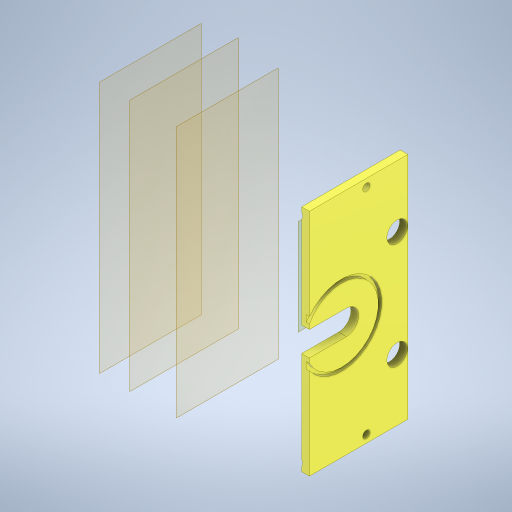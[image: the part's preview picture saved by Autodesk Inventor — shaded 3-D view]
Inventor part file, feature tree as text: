
AUTODESK INVENTOR PART (.ipt)
format: ipt  version: 2023 (Build 270158030, 158C)  size: 688,128 bytes
history: native  units: mm
features: sketch x18, extrude x17, projected_geometry x5, hole x4, plane x3, mirror x2, split x1
ambient origin geometry x8: Origin, YZ Plane, XZ Plane, XY Plane, X Axis, Y Axis, Z Axis, Center Point
bodies: Solid1 (feature_tree)
feature tree (50):
  extrude  "MainInnerBodyExtrusion"  Depth=149.0mm
  extrude  "HoleForCamerabase"  Depth=15.7mm
  extrude  "HoleForFan"  Depth=59.0mm
  extrude  "HoleForPi"  TaperAngle=0.0deg  [1 undecoded]
  extrude  "HoleForPoeAdapter"  Depth=62.0mm
  extrude  "HoleForThermister"  Depth=47.0mm
  extrude  "HoleForSensor"  Depth=32.0mm
  extrude  "SlotsForRearFan"  Depth=47.0mm
  extrude  "VentForCamera"  Depth=16.0mm
  extrude  "HoleForLens"  Depth=118.0mm
  sketch  "Sketch23"  dims[d26=49.0mm d27=118.0mm]
  hole  "Hole for 6-32 Insert"  [1 undecoded]
  hole  "Screw hole for 6-32 screw"  [1 undecoded]
  hole  "Side hole for 1-4 20 insert"  [1 undecoded]
  mirror  "Mirror for side insert"
  extrude  "Extrusion18"  Depth=17.0mm
  extrude  "HoleForPowerWire"  TaperAngle=0.0deg  [1 undecoded]
  extrude  "Extrusion21"  Depth=2.0mm
  extrude  "Extrusion22"  Depth=4.0mm
  extrude  "Extrusion23"  Depth=10.0mm
  extrude  "ExtrusionForBottom"  Depth=10.0mm TaperAngle=0.0deg
  hole  "10-32 holesToBoltFixture"  [1 undecoded]
  plane  "Work Plane1"
  plane  "Work Plane2"
  mirror  "Mirror4"
  extrude  "CutOutForFilter"  Depth=10.0mm
  plane  "Work Plane3"
  split  "Split2"
  sketch  "Sketch1"  dims[d0=222.7mm d1=149.0mm]
  sketch  "Sketch3"  dims[d2=50.0mm d3=0.0mm d5=15.7mm]
  sketch  "Sketch4"  dims[d6=54.0mm d7=59.0mm]
  sketch  "Sketch6"  dims[d8=47.0mm d9=0.0mm]
  sketch  "Sketch7"  dims[d13=16.0mm d14=62.0mm]
  sketch  "Sketch11"  dims[d15=3.0mm d16=47.0mm]
  sketch  "Sketch15"  dims[d17=0.0mm d20=32.0mm]
  sketch  "Sketch16"  dims[d21=129.0mm d22=47.0mm]
  sketch  "Sketch18"  dims[d23=0.0mm d25=16.0mm]
  sketch  "Sketch24"  dims[d28=47.0mm d29=0.0mm]
  sketch  "Sketch25"  dims[d36=69.0mm d37=28.0mm]
  projected_geometry  "Projected Loop1"
  sketch  "Sketch26"  dims[d38=47.0mm d39=0.0mm]
  sketch  "Sketch35"  dims[d42=50.0mm d43=17.0mm]
  sketch  "Sketch37"  dims[d46=31.5mm d47=0.0mm]
  projected_geometry  "Projected Loop3"
  projected_geometry  "Projected Loop4"
  sketch  "Sketch39"  dims[d67=60.0mm d69=2.0mm]
  projected_geometry  "Projected Loop5"
  sketch  "Sketch40"  dims[d71=4.0mm d72=4.0mm]
  sketch  "Sketch43"  dims[d73=4.0mm d75=4.0mm d76=10.0mm d77=0.0mm d78=15.5mm d79=22.0mm d85=3.0mm d86=3.0mm d87=10.0mm d88=16.0mm d89=1.5mm d90=3.0mm d91=3.0mm d92=3.0mm d93=0.0mm d94=0.0mm d95=15.0mm d97=16.0mm d98=10.0mm d99=0.0mm d106=5.0mm d108=5.0mm d109=4.7mm d110=6.0mm d111=5.54mm d112=5.55mm d113=90.0deg d114=7.2mm d115=20.594885mm d116=3.797mm d117=6.0mm d118=12.7mm d119=2.362mm d120=90.0deg d121=15.0mm d122=20.594885mm d130=7.666mm d131=6.0mm d132=8.406mm d133=7.41mm d134=90.0deg d135=9.53mm d136=20.594885mm d137=24.0mm d138=10.0mm d139=3.0mm d140=25.0mm d141=0.0mm d142=30.0mm d144=10.0mm d145=0.0mm d215=4.8514mm d216=5.0mm d217=5.0mm d218=10.0mm d219=10.0mm d220=9.525mm d221=0.0mm d222=76.2mm d223=76.2mm d224=76.2mm d225=76.2mm d226=25.0mm d227=111.350057mm d228=2.0mm d229=0.0mm d230=2.0mm d231=0.0mm d232=14.0mm d233=0.0mm d234=7.0mm d235=40.0mm d236=40.0mm d237=5.105mm d238=6.0mm d239=13.335mm d240=6.35mm d241=90.0deg d242=135.0mm d243=20.594885mm d246=30.0mm d247=-20.0mm d255=21.0mm d256=52.0mm d257=47.5mm d258=2.0mm d259=0.0mm d260=0.0mm]
  projected_geometry  "Projected Loop8"
note: 6 required parameter values undecoded (feature->parameter linkage not recoverable at this tier; creation-order binding heuristic only, values carry confidence <= 0.55)
